# Revit family: EL-EN1497xxWSxxxMRM0500-EDS3
name_source: partatom
category: Oprawy oświetleniowe
units: mm (PartAtom-declared; Revit-internal decimal feet)

## family parameters
Numer OmniClass = 23.80.70.11
Obiekt nadrzędny = Powierzchnia
Punkt obliczania pomieszczeń = Nie
Tnij formami wycięć po wczytaniu = Nie
Typ części = Normalny
Tytuł OmniClass = Luminaries for Internal Lighting
Współdzielony = Nie
Wymiar okrągłego złącza = Użyj średnicy
Źródło światła = Tak

## types (4) — shared parameters
Emituj kształt widoczny w renderingu = Nie
Emituj z długości prostokąta = 1068 mm  [stored 3.50394 ft]
Emituj z szerokości prostokąta = 48 mm  [stored 0.15748 ft]
Filtr koloru = 16777215
Kod zespołu = D5020200
Lampa = LED
Obciążenie pozorne = 44 VA
Odchylenie kierunku = 90.00°
Plik sieci fotometrycznej = EL-xxx_MRM.IES
Producent = RIDI Leuchten GmbH
URL = www.ridi.de
Zmiana temperatury barwowej przyciemniania lampy = <Brak>
brand = RIDI
conformity mark = CE
electrical safety class = 1
height = 60 mm  [stored 0.19685 ft]
ingress protection (IP) code = IP40
length = 1497 mm  [stored 4.91142 ft]
nominal frequency = 50-60Hz
nominal voltage = 230
rated input power = 44
voltage type (AC, DC, UC) = AC
weight = 3,7 kg
width = 115 mm  [stored 0.377297 ft]
zero-valued in all types: Domyślna rzędna

## per-type parameters (varying)
| type | Model |
| EL-EN1497NDWS830MRM0500-EDS3 | 0828003 |
| EL-EN1497DAWS830MRM0500-EDS3 | 0838003 |
| EL-EN1497NDWS840MRM0500-EDS3 | 0828004 |
| EL-EN1497DAWS840MRM0500-EDS3 | 0838004 |

note: column(s) folded — value = type name in every type: product name

note: [stored X ft] marks values corroborated as IEEE doubles in the binary element streams (Revit-internal decimal feet)
